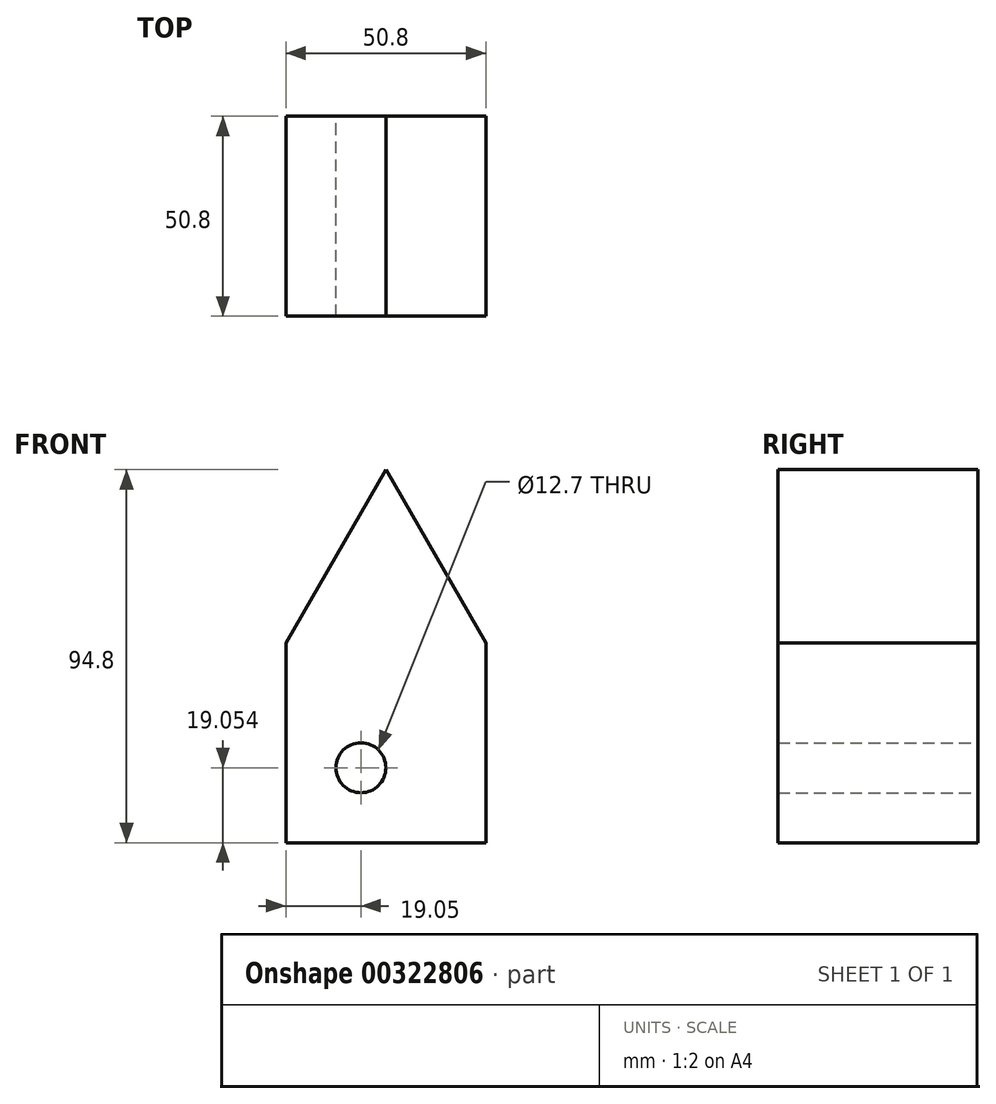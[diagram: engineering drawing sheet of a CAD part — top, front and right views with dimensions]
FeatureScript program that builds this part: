
annotation { "Feature Type Name" : "Feature", "Feature Type Description" : "" }
export const myFeature = defineFeature(function(context is Context, id is Id, definition is map)
    precondition{}
    {
        {
            var Q0;
            Q0=qCreatedBy(makeId("Front.planeOp"),FACE);
            var sketch = newSketch(context, id + "F0", { "sketchPlane" : qUnion([Q0])});
            skLineSegment(sketch, "E0.bottom", {"start": v(-25.4, 30.83) * mm, "end": v(25.4, 30.83) * mm});
            skLineSegment(sketch, "E0.top", {"start": v(-25.4, -19.97) * mm, "end": v(25.4, -19.97) * mm});
            skLineSegment(sketch, "E0.left", {"start": v(-25.4, 30.83) * mm, "end": v(-25.4, -19.97) * mm});
            skLineSegment(sketch, "E0.right", {"start": v(25.4, 30.83) * mm, "end": v(25.4, -19.97) * mm});
            skLineSegment(sketch, "E1", {"start": v(-25.4, 30.83) * mm, "end": v(0, 74.83) * mm});
            skLineSegment(sketch, "E2", {"start": v(25.4, 30.83) * mm, "end": v(0, 74.83) * mm});
            skCircle(sketch, "E3", {"center": v(-6.35, -0.92) * mm, "radius": 6.35 * mm});
            skSolve(sketch);
        }
        {
            var Q0;
            Q0=makeQuery(id+"F0.imprint","IMPRINT",FACE,{"disambiguationData":[TD([[makeQuery(id+"F0.imprint","IMPRINT",EDGE,{"derivedFrom":sQuery(id+"F0.wireOp",EDGE,"E0.bottom")}),1.0]])]});
            var Q1;
            Q1=makeQuery(id+"F0.imprint","IMPRINT",FACE,{"disambiguationData":[TD([[makeQuery(id+"F0.imprint","IMPRINT",EDGE,{"derivedFrom":sQuery(id+"F0.wireOp",EDGE,"E0.bottom")}),-1.0]])]});
            extrude(context, id + "F1", {"entities" : qUnion([Q0, Q1]), "depth" : 50.8 * mm});
        }
    });
